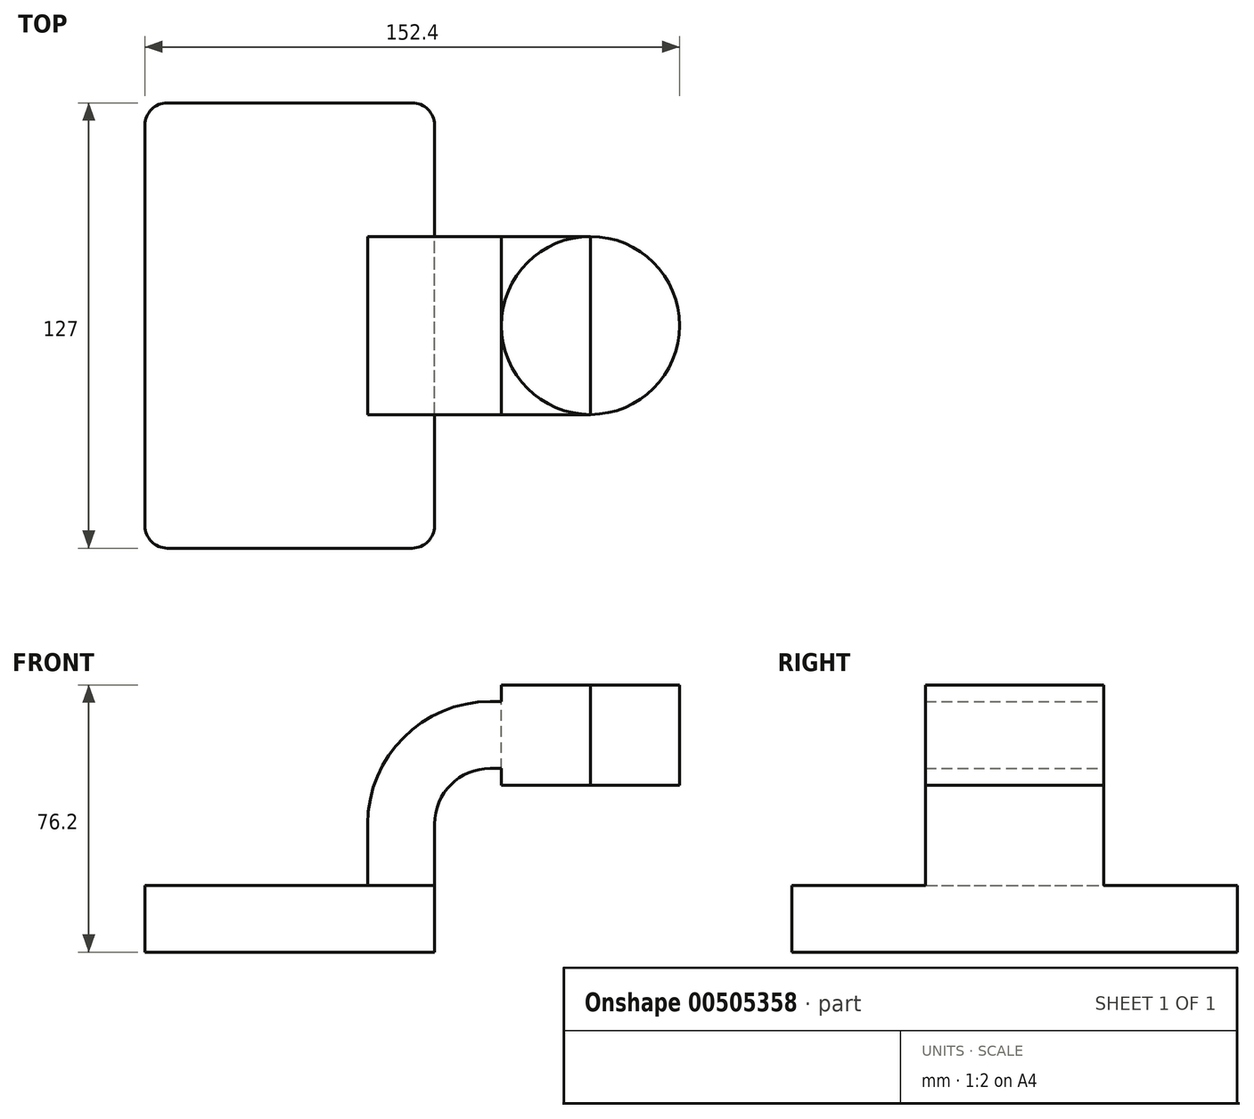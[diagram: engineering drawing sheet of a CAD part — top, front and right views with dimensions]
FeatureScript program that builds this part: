
annotation { "Feature Type Name" : "Feature", "Feature Type Description" : "" }
export const myFeature = defineFeature(function(context is Context, id is Id, definition is map)
    precondition{}
    {
        {
            var Q0;
            Q0=qCreatedBy(makeId("Front.planeOp"),FACE);
            var sketch = newSketch(context, id + "F0", { "sketchPlane" : qUnion([Q0])});
            skLineSegment(sketch, "E0.bottom", {"start": v(41.28, 4.05) * mm, "end": v(-41.28, 4.05) * mm});
            skLineSegment(sketch, "E0.top", {"start": v(41.28, 23.1) * mm, "end": v(-41.28, 23.1) * mm});
            skLineSegment(sketch, "E0.left", {"start": v(41.28, 4.05) * mm, "end": v(41.28, 23.1) * mm});
            skLineSegment(sketch, "E0.right", {"start": v(-41.27, 4.05) * mm, "end": v(-41.28, 23.1) * mm});
            skPoint(sketch, "E0.middle", {"position": v(0, 13.57) * mm});
            skLineSegment(sketch, "E1.bottom", {"start": v(111.12, 51.67) * mm, "end": v(60.32, 51.67) * mm});
            skLineSegment(sketch, "E1.top", {"start": v(111.12, 80.25) * mm, "end": v(60.32, 80.25) * mm});
            skLineSegment(sketch, "E1.left", {"start": v(111.12, 51.67) * mm, "end": v(111.12, 80.25) * mm});
            skLineSegment(sketch, "E1.right", {"start": v(60.32, 51.67) * mm, "end": v(60.32, 80.25) * mm});
            skPoint(sketch, "E1.middle", {"position": v(85.73, 65.96) * mm});
            skLineSegment(sketch, "E2", {"start": v(41.28, 23.1) * mm, "end": v(41.27, 40.57) * mm});
            skArc(sketch, "E3", {"start": v(41.27, 40.57) * mm, "mid": v(45.92, 51.8) * mm, "end": v(57.15, 56.45) * mm});
            skLineSegment(sketch, "E4", {"start": v(57.15, 56.45) * mm, "end": v(85.68, 56.45) * mm});
            skLineSegment(sketch, "E5.0", {"start": v(57.15, 75.5) * mm, "end": v(85.72, 75.5) * mm});
            skArc(sketch, "E5.1", {"start": v(22.23, 40.57) * mm, "mid": v(32.45, 65.27) * mm, "end": v(57.15, 75.5) * mm});
            skLineSegment(sketch, "E5.2", {"start": v(22.23, 23.1) * mm, "end": v(22.22, 40.57) * mm});
            skLineSegment(sketch, "E6", {"start": v(85.72, 80.25) * mm, "end": v(85.72, 51.67) * mm});
            skFitSpline(sketch, "E7", {"points": [v(-41.28, 23.1) * mm, v(60.32, 80.25) * mm], "startDerivative": vector(79.5, 119.64) * mm, "endDerivative": vector(163.71, -4.18) * mm});
            skSolve(sketch);
        }
        {
            var Q0;
            Q0=makeQuery(id+"F0.imprint","IMPRINT",FACE,{"disambiguationData":[TD([[makeQuery(id+"F0.imprint","IMPRINT",EDGE,{"derivedFrom":sQuery(id+"F0.wireOp",EDGE,"E0.bottom")}),-1.0]])]});
            extrude(context, id + "F1", {"entities" : qUnion([Q0]), "endBound" : BoundingType.SYMMETRIC, "depth" : 127 * mm});
        }
        {
            var Q0;
            {var subQ3=sQuery(id+"F0.wireOp",EDGE,"E1.right");var subQ5=sQuery(id+"F0.wireOp",EDGE,"E1.bottom");var subQ6=makeQuery(id+"F0.imprint","INTERSECT",VERTEX,{"derivedFrom":[subQ5,subQ3]});Q0=makeQuery(id+"F0.imprint","IMPRINT",FACE,{"disambiguationData":[TD([[makeQuery(id+"F0.imprint","IMPRINT",EDGE,{"disambiguationData":[TD([[subQ6,1.0]])],"derivedFrom":subQ5}),-1.0]])]});}
            var Q1;
            {var subQ1=sQuery(id+"F0.wireOp",EDGE,"E2");Q1=makeQuery(id+"F0.imprint","IMPRINT",FACE,{"disambiguationData":[TD([[makeQuery(id+"F0.imprint","IMPRINT",EDGE,{"derivedFrom":subQ1}),1.0]])]});}
            var Q2;
            {var subQ3=sQuery(id+"F0.wireOp",EDGE,"E6");var subQ5=sQuery(id+"F0.wireOp",EDGE,"E5.0");var subQ7=makeQuery(id+"F0.imprint","INTERSECT",VERTEX,{"derivedFrom":[subQ5,subQ3]});Q2=makeQuery(id+"F0.imprint","IMPRINT",FACE,{"disambiguationData":[TD([[makeQuery(id+"F0.imprint","IMPRINT",EDGE,{"disambiguationData":[TD([[subQ7,1.0]])],"derivedFrom":subQ5}),1.0]])]});}
            extrude(context, id + "F2", {"entities" : qUnion([Q0, Q1, Q2]), "operationType" : NewBodyOperationType.ADD, "endBound" : BoundingType.SYMMETRIC, "depth" : 50.8 * mm});
        }
        {
            var Q0;
            {var subQ0=sQuery(id+"F0.wireOp",EDGE,"E5.1");Q0=makeQuery(id+"F0.imprint","IMPRINT",FACE,{"disambiguationData":[TD([[makeQuery(id+"F0.imprint","IMPRINT",EDGE,{"derivedFrom":subQ0}),1.0]])]});}
            extrude(context, id + "F3", {"entities" : qUnion([Q0]), "operationType" : NewBodyOperationType.ADD, "endBound" : BoundingType.SYMMETRIC, "depth" : 19.05 * mm});
        }
        {
            var Q0;
            {var subQ0=sQuery(id+"F0.wireOp",EDGE,"E1.left");Q0=makeQuery(id+"F0.imprint","IMPRINT",FACE,{"disambiguationData":[TD([[makeQuery(id+"F0.imprint","IMPRINT",EDGE,{"derivedFrom":subQ0}),1.0]])]});}
            var Q1;
            Q1=sQuery(id+"F0.wireOp",EDGE,"E6");
            revolve(context, id + "F4", {"entities" : qUnion([Q0]), "axis" : qUnion([Q1]), "revolveType" : RevolveType.FULL});
        }
        {
            var Q0;
            Q0=makeQuery(id+"F1.opExtrude","CAP_EDGE",EDGE,{"disambiguationData":[OSD([sQuery(id+"F0.wireOp",EDGE,"E0.left")])],"isStart":true});
            var Q1;
            Q1=makeQuery(id+"F1.opExtrude","CAP_EDGE",EDGE,{"disambiguationData":[OSD([sQuery(id+"F0.wireOp",EDGE,"E0.right")])],"isStart":true});
            var Q2;
            Q2=makeQuery(id+"F1.opExtrude","CAP_EDGE",EDGE,{"disambiguationData":[OSD([sQuery(id+"F0.wireOp",EDGE,"E0.left")])],"isStart":false});
            var Q3;
            Q3=makeQuery(id+"F1.opExtrude","CAP_EDGE",EDGE,{"disambiguationData":[OSD([sQuery(id+"F0.wireOp",EDGE,"E0.right")])],"isStart":false});
            fillet(context, id + "F5", {"entities" : qUnion([Q0, Q1, Q2, Q3]), "radius" : 6.35 * mm, "tangentPropagation" : true, "allowEdgeOverflow" : false});
        }
    });
